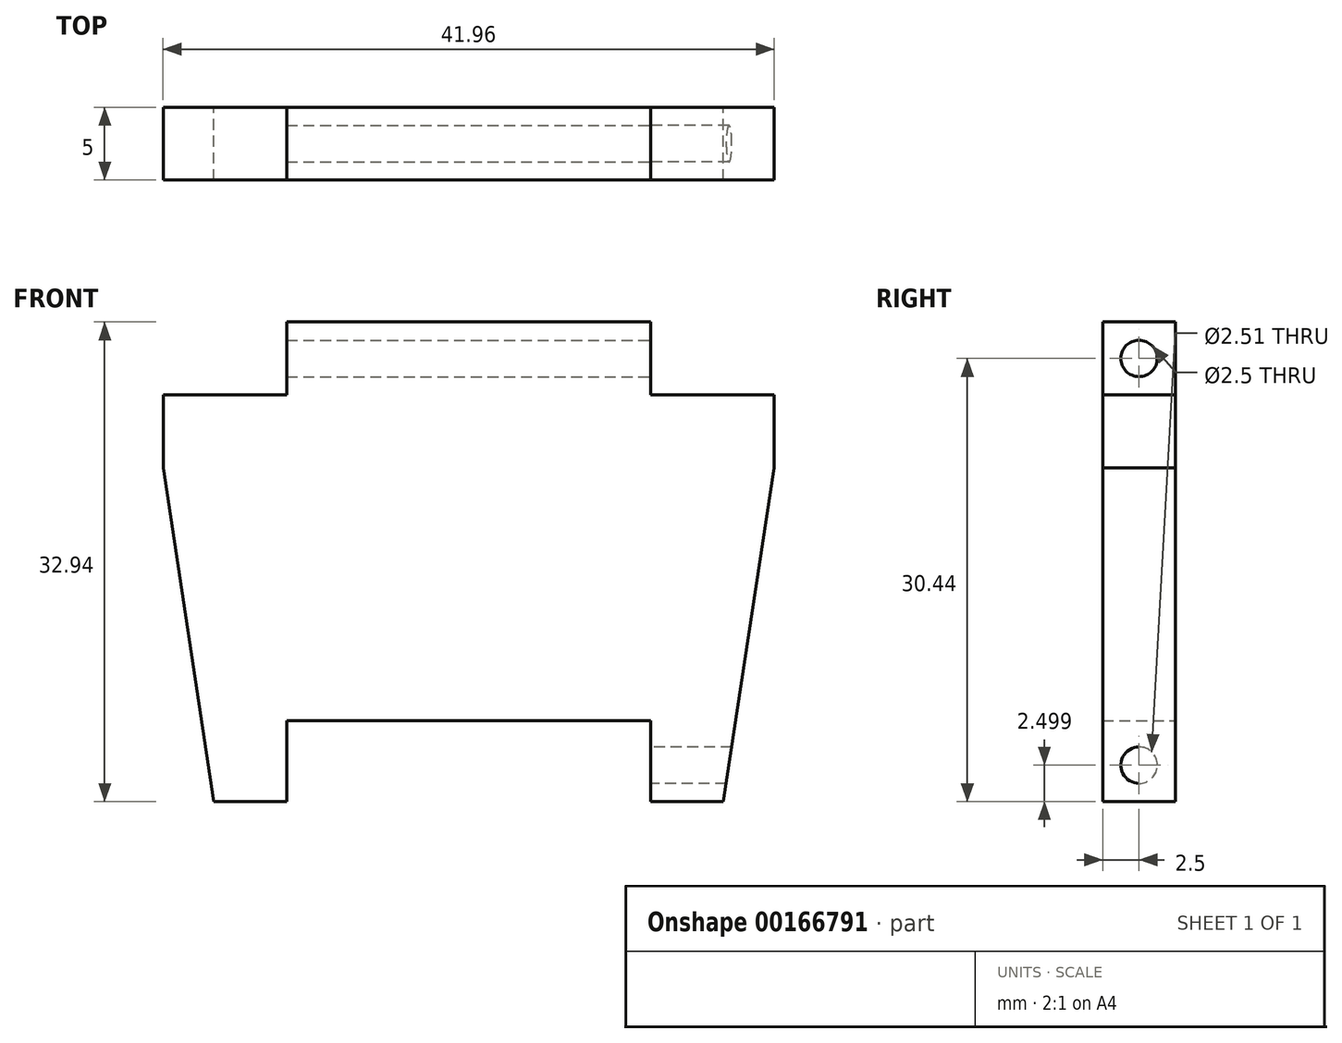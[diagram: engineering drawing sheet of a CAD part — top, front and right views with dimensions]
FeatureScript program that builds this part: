
annotation { "Feature Type Name" : "Feature", "Feature Type Description" : "" }
export const myFeature = defineFeature(function(context is Context, id is Id, definition is map)
    precondition{}
    {
        {
            var Q0;
            Q0=qCreatedBy(makeId("Front.planeOp"),FACE);
            var sketch = newSketch(context, id + "F0", { "sketchPlane" : qUnion([Q0])});
            skLineSegment(sketch, "E0", {"start": v(-12.04, -32.44) * mm, "end": v(12.96, -32.44) * mm});
            skLineSegment(sketch, "E1", {"start": v(-12.04, -32.44) * mm, "end": v(-12.04, -37.98) * mm});
            skLineSegment(sketch, "E2", {"start": v(-12.04, -37.98) * mm, "end": v(-17.04, -37.98) * mm});
            skLineSegment(sketch, "E3", {"start": v(-17.04, -37.98) * mm, "end": v(-20.52, -15.06) * mm});
            skLineSegment(sketch, "E4", {"start": v(-20.52, -15.06) * mm, "end": v(-20.52, -10.04) * mm});
            skLineSegment(sketch, "E5", {"start": v(-20.52, -10.04) * mm, "end": v(-12.04, -10.04) * mm});
            skLineSegment(sketch, "E6", {"start": v(-12.04, -10.04) * mm, "end": v(-12.04, -5.04) * mm});
            skPoint(sketch, "E6.endSnap0", {"position": v(-12.04, -35.2) * mm});
            skLineSegment(sketch, "E7", {"start": v(-12.04, -5.04) * mm, "end": v(12.96, -5.04) * mm});
            skLineSegment(sketch, "E8", {"start": v(12.96, -5.04) * mm, "end": v(12.96, -10.04) * mm});
            skLineSegment(sketch, "E9", {"start": v(12.96, -32.44) * mm, "end": v(12.96, -37.98) * mm});
            skLineSegment(sketch, "E10", {"start": v(12.96, -37.98) * mm, "end": v(17.96, -37.98) * mm});
            skLineSegment(sketch, "E11", {"start": v(17.96, -37.98) * mm, "end": v(21.44, -15.06) * mm});
            skLineSegment(sketch, "E12", {"start": v(21.44, -15.06) * mm, "end": v(21.44, -10.04) * mm});
            skLineSegment(sketch, "E13", {"start": v(21.44, -10.04) * mm, "end": v(12.96, -10.04) * mm});
            skSolve(sketch);
        }
        {
            var Q0;
            Q0=makeQuery(id+"F0.imprint","IMPRINT",FACE,{"disambiguationData":[TD([[makeQuery(id+"F0.imprint","IMPRINT",EDGE,{"derivedFrom":sQuery(id+"F0.wireOp",EDGE,"E0")}),1.0]])]});
            extrude(context, id + "F1", {"entities" : qUnion([Q0]), "depth" : 5 * mm});
        }
        {
            var Q0;
            Q0=makeQuery(id+"F1.opExtrude","SWEPT_FACE",FACE,{"disambiguationData":[OSD([sQuery(id+"F0.wireOp",EDGE,"E9")])]});
            var sketch = newSketch(context, id + "F2", { "sketchPlane" : qUnion([Q0])});
            skCircle(sketch, "E14", {"center": v(2.5, -35.48) * mm, "radius": 1.25 * mm});
            skSolve(sketch);
        }
        {
            var Q0;
            Q0=makeQuery(id+"F2.imprint","IMPRINT",FACE,{"disambiguationData":[TD([[makeQuery(id+"F2.imprint","IMPRINT",EDGE,{"derivedFrom":sQuery(id+"F2.wireOp",EDGE,"E14")}),1.0]])]});
            extrude(context, id + "F3", {"entities" : qUnion([Q0]), "operationType" : NewBodyOperationType.REMOVE, "oppositeDirection" : true, "depth" : 25 * mm});
        }
        {
            var Q0;
            Q0=makeQuery(id+"F1.opExtrude","SWEPT_FACE",FACE,{"disambiguationData":[OSD([sQuery(id+"F0.wireOp",EDGE,"E8")])]});
            var sketch = newSketch(context, id + "F4", { "sketchPlane" : qUnion([Q0])});
            skCircle(sketch, "E15", {"center": v(-2.5, -7.54) * mm, "radius": 1.25 * mm});
            skSolve(sketch);
        }
        {
            var Q0;
            Q0=makeQuery(id+"F4.imprint","IMPRINT",FACE,{"disambiguationData":[TD([[makeQuery(id+"F4.imprint","IMPRINT",EDGE,{"derivedFrom":sQuery(id+"F4.wireOp",EDGE,"E15")}),1.0]])]});
            extrude(context, id + "F5", {"entities" : qUnion([Q0]), "operationType" : NewBodyOperationType.REMOVE, "oppositeDirection" : true, "depth" : 25 * mm});
        }
    });
